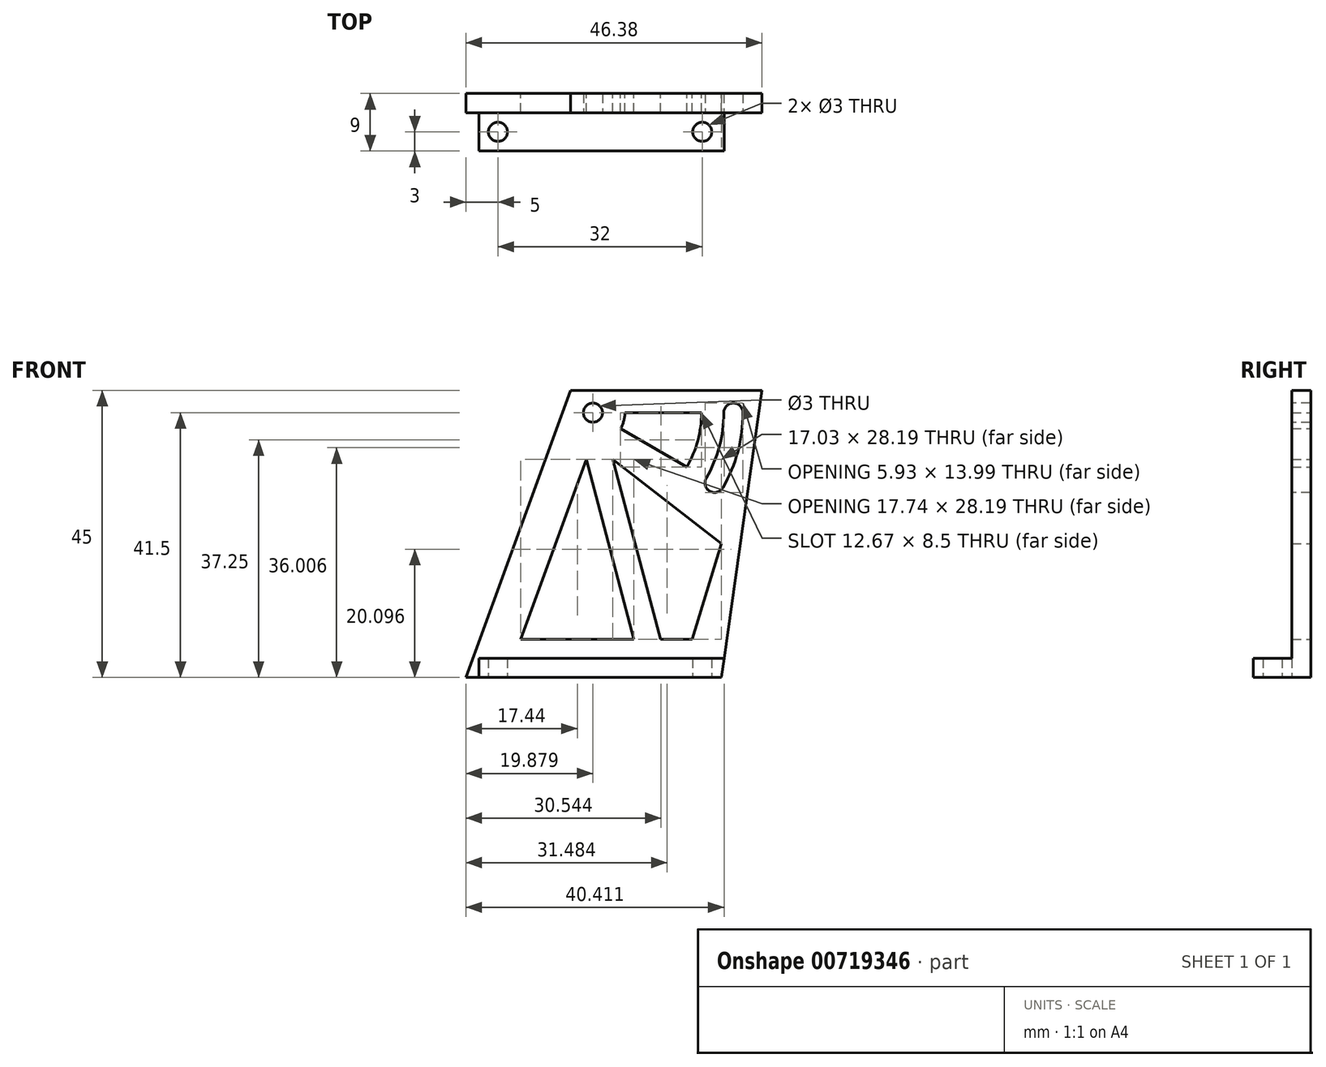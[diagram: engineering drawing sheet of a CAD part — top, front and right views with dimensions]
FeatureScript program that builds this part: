
annotation { "Feature Type Name" : "Feature", "Feature Type Description" : "" }
export const myFeature = defineFeature(function(context is Context, id is Id, definition is map)
    precondition{}
    {
        {
            var Q0;
            Q0=qCreatedBy(makeId("Front.planeOp"),FACE);
            var sketch = newSketch(context, id + "F0", { "sketchPlane" : qUnion([Q0])});
            skLineSegment(sketch, "E0", {"start": v(0, 0) * mm, "end": v(40, 0) * mm});
            skLineSegment(sketch, "E1", {"start": v(40, 0) * mm, "end": v(46.38, 45) * mm});
            skLineSegment(sketch, "E2", {"start": v(46.38, 45) * mm, "end": v(16.38, 45) * mm});
            skLineSegment(sketch, "E3", {"start": v(16.38, 45) * mm, "end": v(0, 0) * mm});
            skCircle(sketch, "E4", {"center": v(19.88, 41.5) * mm, "radius": 1.5 * mm});
            skArc(sketch, "E5", {"start": v(40.23, 29.75) * mm, "mid": v(42.58, 35.42) * mm, "end": v(43.38, 41.5) * mm});
            skArc(sketch, "E6", {"start": v(37.63, 31.25) * mm, "mid": v(39.68, 36.2) * mm, "end": v(40.38, 41.5) * mm});
            skArc(sketch, "E7", {"start": v(43.38, 41.5) * mm, "mid": v(41.88, 43) * mm, "end": v(40.38, 41.5) * mm});
            skArc(sketch, "E8", {"start": v(37.63, 31.25) * mm, "mid": v(38.18, 29.2) * mm, "end": v(40.23, 29.75) * mm});
            skSolve(sketch);
        }
        {
            var Q0;
            Q0=qSketchRegion(id+"F0",true);
            extrude(context, id + "F1", {"entities" : qUnion([Q0]), "depth" : 3 * mm, "offsetDistance" : 25 * mm});
        }
        {
            var Q0;
            Q0=makeQuery(id+"F1.opExtrude","CAP_FACE",FACE,{"disambiguationData":[OSD([sQuery(id+"F0.wireOp",EDGE,"E0"),sQuery(id+"F0.wireOp",EDGE,"E1"),sQuery(id+"F0.wireOp",EDGE,"E2"),sQuery(id+"F0.wireOp",EDGE,"E3"),sQuery(id+"F0.wireOp",EDGE,"E4"),sQuery(id+"F0.wireOp",EDGE,"E5"),sQuery(id+"F0.wireOp",EDGE,"E6"),sQuery(id+"F0.wireOp",EDGE,"E7"),sQuery(id+"F0.wireOp",EDGE,"E8")])],"isStart":true});
            var sketch = newSketch(context, id + "F2", { "sketchPlane" : qUnion([Q0])});
            skLineSegment(sketch, "E9", {"start": v(-40, 0) * mm, "end": v(-40.43, 3) * mm});
            skLineSegment(sketch, "E10", {"start": v(-40.43, 3) * mm, "end": v(-2, 3) * mm});
            skLineSegment(sketch, "E11", {"start": v(-2, 3) * mm, "end": v(-2, 0) * mm});
            skLineSegment(sketch, "E12", {"start": v(-2, 0) * mm, "end": v(-40, 0) * mm});
            skSolve(sketch);
        }
        {
            var Q0;
            Q0=qSketchRegion(id+"F2",true);
            extrude(context, id + "F3", {"entities" : qUnion([Q0]), "operationType" : NewBodyOperationType.ADD, "depth" : 6 * mm, "offsetDistance" : 25 * mm});
        }
        {
            var Q0;
            Q0=makeQuery(id+"F3.boolean.opBoolean","MERGE",FACE,{"derivedFrom":[makeQuery(id+"F1.opExtrude","SWEPT_FACE",FACE,{"disambiguationData":[OSD([sQuery(id+"F0.wireOp",EDGE,"E0")])]}),makeQuery(id+"F3.opExtrude","SWEPT_FACE",FACE,{"disambiguationData":[OSD([sQuery(id+"F2.wireOp",EDGE,"E12")])]})]});
            var sketch = newSketch(context, id + "F4", { "sketchPlane" : qUnion([Q0])});
            skCircle(sketch, "E13", {"center": v(37, -3) * mm, "radius": 1.5 * mm});
            skCircle(sketch, "E14", {"center": v(5, -3) * mm, "radius": 1.5 * mm});
            skSolve(sketch);
        }
        {
            var Q0;
            Q0=qSketchRegion(id+"F4",true);
            extrude(context, id + "F5", {"entities" : qUnion([Q0]), "operationType" : NewBodyOperationType.REMOVE, "oppositeDirection" : true, "depth" : 25 * mm, "offsetDistance" : 25 * mm});
        }
        {
            var Q0;
            Q0=makeQuery(id+"F1.opExtrude","CAP_FACE",FACE,{"disambiguationData":[OSD([sQuery(id+"F0.wireOp",EDGE,"E0"),sQuery(id+"F0.wireOp",EDGE,"E1"),sQuery(id+"F0.wireOp",EDGE,"E2"),sQuery(id+"F0.wireOp",EDGE,"E3"),sQuery(id+"F0.wireOp",EDGE,"E4"),sQuery(id+"F0.wireOp",EDGE,"E5"),sQuery(id+"F0.wireOp",EDGE,"E6"),sQuery(id+"F0.wireOp",EDGE,"E7"),sQuery(id+"F0.wireOp",EDGE,"E8")])],"isStart":false});
            var sketch = newSketch(context, id + "F6", { "sketchPlane" : qUnion([Q0])});
            skLineSegment(sketch, "E15", {"start": v(8.57, 6) * mm, "end": v(18.83, 34.2) * mm});
            skLineSegment(sketch, "E16", {"start": v(18.83, 34.2) * mm, "end": v(26.31, 6) * mm});
            skLineSegment(sketch, "E17", {"start": v(26.31, 6) * mm, "end": v(8.57, 6) * mm});
            skLineSegment(sketch, "E18", {"start": v(22.97, 34.2) * mm, "end": v(30.45, 6) * mm});
            skLineSegment(sketch, "E19", {"start": v(30.45, 6) * mm, "end": v(35.45, 6) * mm});
            skLineSegment(sketch, "E20", {"start": v(35.45, 6) * mm, "end": v(40, 21) * mm});
            skLineSegment(sketch, "E21", {"start": v(40, 21) * mm, "end": v(22.97, 34.2) * mm});
            skArc(sketch, "E22", {"start": v(24.2, 39) * mm, "mid": v(24.7, 40.2) * mm, "end": v(24.88, 41.5) * mm});
            skLineSegment(sketch, "E23", {"start": v(24.88, 41.5) * mm, "end": v(36.88, 41.5) * mm});
            skLineSegment(sketch, "E24", {"start": v(24.2, 39) * mm, "end": v(34.6, 33) * mm});
            skArc(sketch, "E25.trimOffspring", {"start": v(34.6, 33) * mm, "mid": v(36.3, 37.1) * mm, "end": v(36.88, 41.5) * mm});
            skPoint(sketch, "E26.orphan", {"position": v(38.93, 30.5) * mm});
            skSolve(sketch);
        }
        {
            var Q0;
            Q0=qSketchRegion(id+"F6",true);
            extrude(context, id + "F7", {"entities" : qUnion([Q0]), "operationType" : NewBodyOperationType.REMOVE, "oppositeDirection" : true, "depth" : 25 * mm, "offsetDistance" : 25 * mm});
        }
        {
            var Q0;
            Q0=makeQuery(id+"F1.opExtrude","SWEPT_BODY",BODY,{"disambiguationData":[OSD([sQuery(id+"F0.wireOp",EDGE,"E0"),sQuery(id+"F0.wireOp",EDGE,"E1"),sQuery(id+"F0.wireOp",EDGE,"E2"),sQuery(id+"F0.wireOp",EDGE,"E3"),sQuery(id+"F0.wireOp",EDGE,"E4"),sQuery(id+"F0.wireOp",EDGE,"E5"),sQuery(id+"F0.wireOp",EDGE,"E6"),sQuery(id+"F0.wireOp",EDGE,"E7"),sQuery(id+"F0.wireOp",EDGE,"E8")])]});
            var Q1;
            Q1=makeQuery(id+"F1.opExtrude","CAP_FACE",FACE,{"disambiguationData":[OSD([sQuery(id+"F0.wireOp",EDGE,"E0"),sQuery(id+"F0.wireOp",EDGE,"E1"),sQuery(id+"F0.wireOp",EDGE,"E2"),sQuery(id+"F0.wireOp",EDGE,"E3"),sQuery(id+"F0.wireOp",EDGE,"E4"),sQuery(id+"F0.wireOp",EDGE,"E5"),sQuery(id+"F0.wireOp",EDGE,"E6"),sQuery(id+"F0.wireOp",EDGE,"E7"),sQuery(id+"F0.wireOp",EDGE,"E8")])],"isStart":false});
            mirror(context, id + "F8", {"entities" : qUnion([Q0]), "mirrorPlane" : qUnion([Q1])});
        }
        {
            var Q0;
            Q0=makeQuery(id+"F1.opExtrude","SWEPT_BODY",BODY,{"disambiguationData":[OSD([sQuery(id+"F0.wireOp",EDGE,"E0"),sQuery(id+"F0.wireOp",EDGE,"E1"),sQuery(id+"F0.wireOp",EDGE,"E2"),sQuery(id+"F0.wireOp",EDGE,"E3"),sQuery(id+"F0.wireOp",EDGE,"E4"),sQuery(id+"F0.wireOp",EDGE,"E5"),sQuery(id+"F0.wireOp",EDGE,"E6"),sQuery(id+"F0.wireOp",EDGE,"E7"),sQuery(id+"F0.wireOp",EDGE,"E8")])]});
            deleteBodies(context, id + "F9", {"entities" : qUnion([Q0])});
        }
    });
